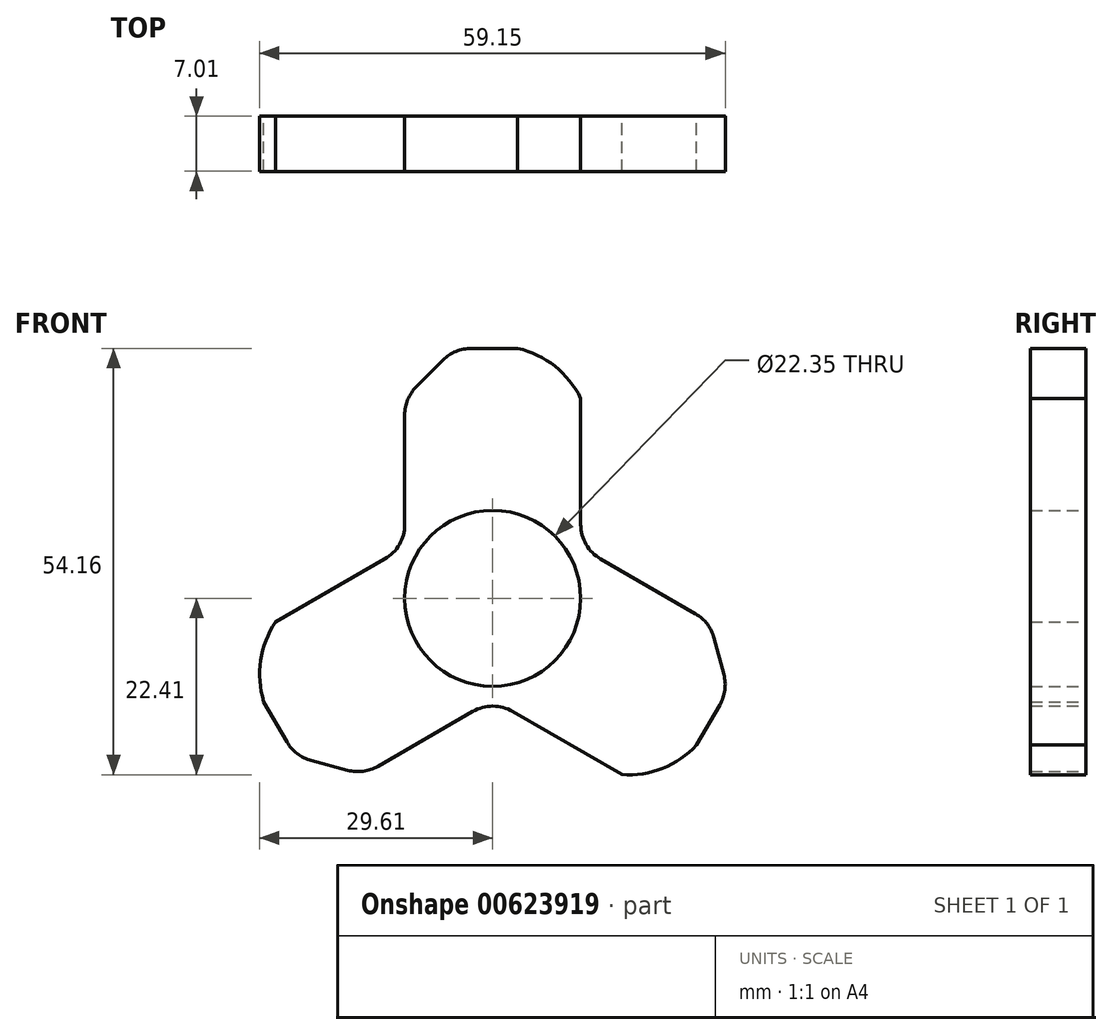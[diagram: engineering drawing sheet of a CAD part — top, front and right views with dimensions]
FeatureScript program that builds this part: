
annotation { "Feature Type Name" : "Feature", "Feature Type Description" : "" }
export const myFeature = defineFeature(function(context is Context, id is Id, definition is map)
    precondition{}
    {
        {
            var Q0;
            Q0=qCreatedBy(makeId("Front.planeOp"),FACE);
            var sketch = newSketch(context, id + "F0", { "sketchPlane" : qUnion([Q0])});
            skCircle(sketch, "E0", {"center": v(0, 0) * mm, "radius": 11.18 * mm});
            skPoint(sketch, "E1.endSnap0", {"position": v(8.14, 0) * mm});
            skLineSegment(sketch, "E2", {"start": v(-11.18, 6.45) * mm, "end": v(-11.18, 25.4) * mm});
            skLineSegment(sketch, "E3", {"start": v(11.18, 6.45) * mm, "end": v(11.18, 25.4) * mm});
            skLineSegment(sketch, "E4", {"start": v(-4.83, 31.75) * mm, "end": v(3.17, 31.75) * mm});
            skLineSegment(sketch, "E5", {"start": v(-11.18, 25.4) * mm, "end": v(-4.83, 31.75) * mm});
            skArc(sketch, "E6", {"start": v(11.18, 25.4) * mm, "mid": v(7.9, 29.49) * mm, "end": v(3.18, 31.75) * mm});
            skPoint(sketch, "E7.orphan", {"position": v(11.18, 31.75) * mm});
            skLineSegment(sketch, "E8.1.0", {"start": v(11.18, 6.45) * mm, "end": v(27.59, -3.02) * mm});
            skLineSegment(sketch, "E8.1.1", {"start": v(27.59, -3.02) * mm, "end": v(29.9, -11.7) * mm});
            skLineSegment(sketch, "E8.1.2", {"start": v(29.9, -11.7) * mm, "end": v(25.9, -18.62) * mm});
            skArc(sketch, "E8.1.3", {"start": v(16.4, -22.38) * mm, "mid": v(21.59, -21.58) * mm, "end": v(25.9, -18.62) * mm});
            skLineSegment(sketch, "E8.1.4", {"start": v(0, -12.9) * mm, "end": v(16.4, -22.38) * mm});
            skLineSegment(sketch, "E8.2.0", {"start": v(0, -12.9) * mm, "end": v(-16.4, -22.38) * mm});
            skLineSegment(sketch, "E8.2.1", {"start": v(-16.4, -22.38) * mm, "end": v(-25.08, -20.05) * mm});
            skLineSegment(sketch, "E8.2.2", {"start": v(-25.08, -20.05) * mm, "end": v(-29.08, -13.13) * mm});
            skArc(sketch, "E8.2.3", {"start": v(-27.59, -3.02) * mm, "mid": v(-29.49, -7.9) * mm, "end": v(-29.08, -13.13) * mm});
            skLineSegment(sketch, "E8.2.4", {"start": v(-11.18, 6.45) * mm, "end": v(-27.59, -3.02) * mm});
            skPoint(sketch, "E9.orphan", {"position": v(-5.59, -9.68) * mm});
            skPoint(sketch, "E10.orphan", {"position": v(16.28, 0) * mm});
            skPoint(sketch, "E11.orphan", {"position": v(-5.59, 9.68) * mm});
            skPoint(sketch, "E12.orphan", {"position": v(5.59, 9.68) * mm});
            skPoint(sketch, "E13.orphan", {"position": v(11.18, 0) * mm});
            skPoint(sketch, "E14.orphan", {"position": v(-27.1, 0) * mm});
            skSolve(sketch);
        }
        {
            var Q0;
            Q0=makeQuery(id+"F0.imprint","IMPRINT",FACE,{"disambiguationData":[TD([[makeQuery(id+"F0.imprint","IMPRINT",EDGE,{"derivedFrom":sQuery(id+"F0.wireOp",EDGE,"E0")}),-1.0]])]});
            extrude(context, id + "F1", {"entities" : qUnion([Q0]), "depth" : 7 * mm, "offsetDistance" : 25.4 * mm});
        }
        {
            var Q0;
            Q0=makeQuery(id+"F1.opExtrude","SWEPT_EDGE",EDGE,{"disambiguationData":[OSD([sQuery(id+"F0.wireOp",EDGE,"E2"),sQuery(id+"F0.wireOp",EDGE,"E8.2.4")])]});
            var Q1;
            Q1=makeQuery(id+"F1.opExtrude","SWEPT_EDGE",EDGE,{"disambiguationData":[OSD([sQuery(id+"F0.wireOp",EDGE,"E2"),sQuery(id+"F0.wireOp",EDGE,"E5")])]});
            var Q2;
            Q2=makeQuery(id+"F1.opExtrude","SWEPT_EDGE",EDGE,{"disambiguationData":[OSD([sQuery(id+"F0.wireOp",EDGE,"E3"),sQuery(id+"F0.wireOp",EDGE,"E8.1.0")])]});
            var Q3;
            Q3=makeQuery(id+"F1.opExtrude","SWEPT_EDGE",EDGE,{"disambiguationData":[OSD([sQuery(id+"F0.wireOp",EDGE,"E8.1.1"),sQuery(id+"F0.wireOp",EDGE,"E8.1.2")])]});
            var Q4;
            Q4=makeQuery(id+"F1.opExtrude","SWEPT_EDGE",EDGE,{"disambiguationData":[OSD([sQuery(id+"F0.wireOp",EDGE,"E8.1.0"),sQuery(id+"F0.wireOp",EDGE,"E8.1.1")])]});
            var Q5;
            Q5=makeQuery(id+"F1.opExtrude","SWEPT_EDGE",EDGE,{"disambiguationData":[OSD([sQuery(id+"F0.wireOp",EDGE,"E8.1.4"),sQuery(id+"F0.wireOp",EDGE,"E8.2.0")])]});
            var Q6;
            Q6=makeQuery(id+"F1.opExtrude","SWEPT_EDGE",EDGE,{"disambiguationData":[OSD([sQuery(id+"F0.wireOp",EDGE,"E8.2.0"),sQuery(id+"F0.wireOp",EDGE,"E8.2.1")])]});
            var Q7;
            Q7=makeQuery(id+"F1.opExtrude","SWEPT_EDGE",EDGE,{"disambiguationData":[OSD([sQuery(id+"F0.wireOp",EDGE,"E8.2.1"),sQuery(id+"F0.wireOp",EDGE,"E8.2.2")])]});
            var Q8;
            Q8=makeQuery(id+"F1.opExtrude","SWEPT_EDGE",EDGE,{"disambiguationData":[OSD([sQuery(id+"F0.wireOp",EDGE,"E4"),sQuery(id+"F0.wireOp",EDGE,"E5")])]});
            fillet(context, id + "F2", {"entities" : qUnion([Q0, Q1, Q2, Q3, Q4, Q5, Q6, Q7, Q8]), "radius" : 5.08 * mm, "tangentPropagation" : true, "allowEdgeOverflow" : false});
        }
    });
